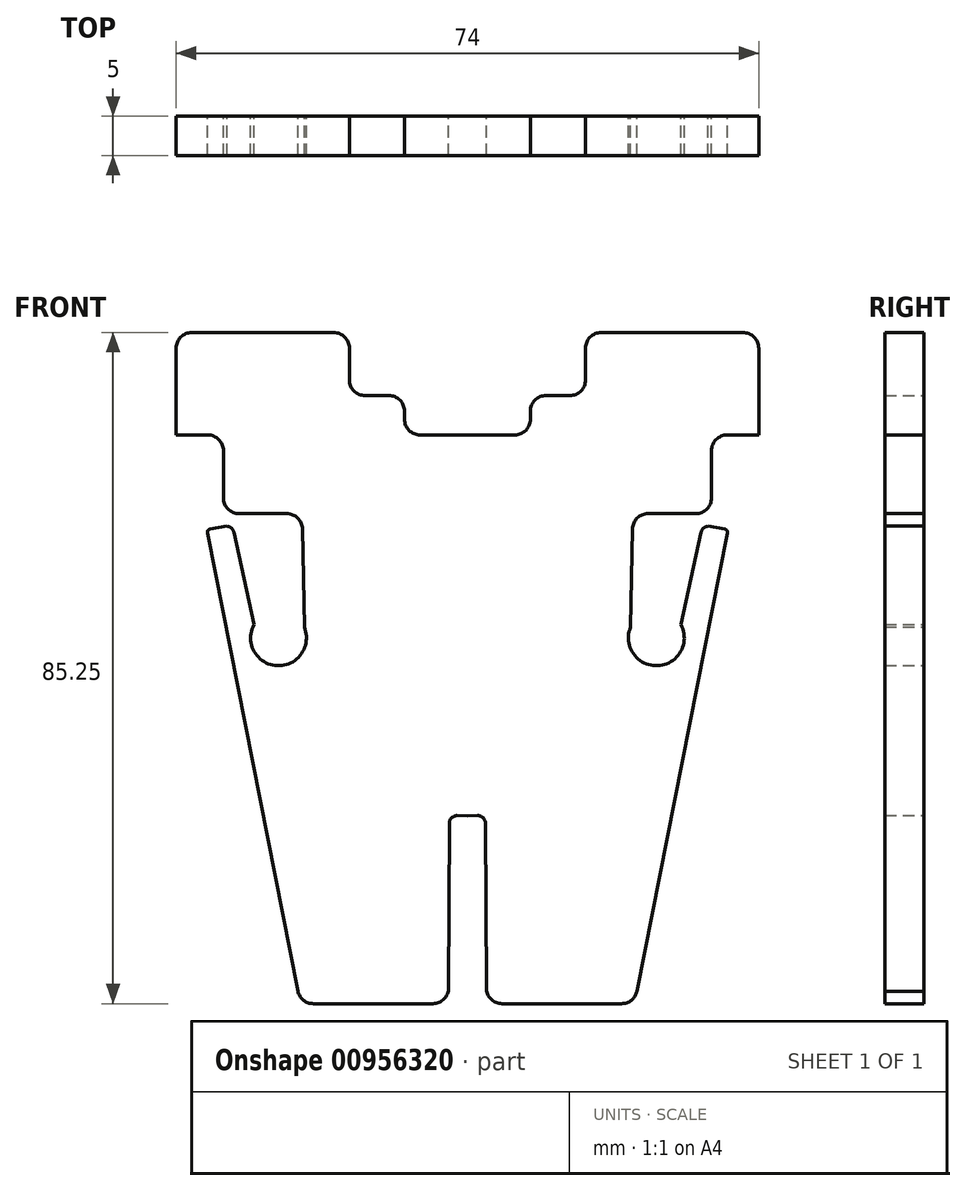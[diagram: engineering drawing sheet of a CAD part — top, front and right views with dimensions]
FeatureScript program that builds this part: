
annotation { "Feature Type Name" : "Feature", "Feature Type Description" : "" }
export const myFeature = defineFeature(function(context is Context, id is Id, definition is map)
    precondition{}
    {
        {
            var Q0;
            Q0=qCreatedBy(makeId("Front.planeOp"),FACE);
            var sketch = newSketch(context, id + "F0", { "sketchPlane" : qUnion([Q0])});
            skLineSegment(sketch, "E0", {"start": v(-4.4, -46.48) * mm, "end": v(-19.58, -46.48) * mm});
            skLineSegment(sketch, "E1", {"start": v(-22.96, 15.77) * mm, "end": v(-29, 15.77) * mm});
            skLineSegment(sketch, "E2", {"start": v(-31, 17.77) * mm, "end": v(-31, 23.77) * mm});
            skLineSegment(sketch, "E3", {"start": v(-33, 25.77) * mm, "end": v(-37, 25.77) * mm});
            skLineSegment(sketch, "E4", {"start": v(-37, 25.77) * mm, "end": v(-37, 36.77) * mm});
            skLineSegment(sketch, "E5", {"start": v(-35, 38.77) * mm, "end": v(-17, 38.77) * mm});
            skLineSegment(sketch, "E6", {"start": v(-15, 36.77) * mm, "end": v(-15, 32.77) * mm});
            skLineSegment(sketch, "E7", {"start": v(-13, 30.77) * mm, "end": v(-10, 30.77) * mm});
            skLineSegment(sketch, "E8", {"start": v(-8, 28.77) * mm, "end": v(-8, 27.77) * mm});
            skLineSegment(sketch, "E9", {"start": v(-6, 25.77) * mm, "end": v(0, 25.77) * mm});
            skLineSegment(sketch, "E10.MirrorCS", {"start": v(6, 25.77) * mm, "end": v(0, 25.77) * mm});
            skLineSegment(sketch, "E11.MirrorCS", {"start": v(13, 30.77) * mm, "end": v(10, 30.77) * mm});
            skLineSegment(sketch, "E12.MirrorCS", {"start": v(15, 36.77) * mm, "end": v(15, 32.77) * mm});
            skLineSegment(sketch, "E13.MirrorCS", {"start": v(35, 38.77) * mm, "end": v(17, 38.77) * mm});
            skLineSegment(sketch, "E14.MirrorCS", {"start": v(37, 25.77) * mm, "end": v(37, 36.77) * mm});
            skLineSegment(sketch, "E15.MirrorCS", {"start": v(22.96, 15.77) * mm, "end": v(29, 15.77) * mm});
            skLineSegment(sketch, "E16.MirrorCS", {"start": v(31, 17.77) * mm, "end": v(31, 23.77) * mm});
            skLineSegment(sketch, "E17.MirrorCS", {"start": v(33, 25.77) * mm, "end": v(37, 25.77) * mm});
            skLineSegment(sketch, "E18.MirrorCS", {"start": v(8, 28.77) * mm, "end": v(8, 27.77) * mm});
            skPoint(sketch, "E19.orphan", {"position": v(-2.04, -46.48) * mm});
            skPoint(sketch, "E20.MirrorCS.end.orphan", {"position": v(30.95, 9.46) * mm});
            skPoint(sketch, "E20.MirrorCS.start.orphan", {"position": v(20.96, -46.48) * mm});
            skPoint(sketch, "E21.orphan", {"position": v(-30.95, 9.46) * mm});
            skPoint(sketch, "E22.trimOffspring.end.orphan", {"position": v(20.62, -4.11) * mm});
            skLineSegment(sketch, "E23.trimOffspring", {"start": v(20.72, 1.3) * mm, "end": v(20.96, 13.81) * mm});
            skPoint(sketch, "E24.MirrorCS.start.orphan", {"position": v(20.73, -4.43) * mm});
            skPoint(sketch, "E25.orphan", {"position": v(-20.73, -4.43) * mm});
            skLineSegment(sketch, "E26.trimOffspring", {"start": v(-20.72, 1.3) * mm, "end": v(-20.96, 13.81) * mm});
            skPoint(sketch, "E27.start.orphan", {"position": v(-20.62, -4.11) * mm});
            skPoint(sketch, "E28.end.orphan", {"position": v(-20.7, -4.48) * mm});
            skPoint(sketch, "E29.MirrorCS.end.orphan", {"position": v(20.7, -4.48) * mm});
            skPoint(sketch, "E30.MirrorCS.start.orphan", {"position": v(-4, -24.4) * mm});
            skPoint(sketch, "E31.orphan", {"position": v(2.04, -46.48) * mm});
            skPoint(sketch, "E32.MirrorCS.start.orphan", {"position": v(0, -24.4) * mm});
            skPoint(sketch, "E33.end.orphan", {"position": v(4, -24.4) * mm});
            skArc(sketch, "E34", {"start": v(-27.13, 1.67) * mm, "mid": v(-24.16, -3.54) * mm, "end": v(-20.73, 1.37) * mm});
            skLineSegment(sketch, "E35.MirrorCS", {"start": v(27.13, 1.67) * mm, "end": v(27.1, 1.59) * mm});
            skArc(sketch, "E36.MirrorC", {"start": v(27.13, 1.67) * mm, "mid": v(24.16, -3.54) * mm, "end": v(20.73, 1.37) * mm});
            skPoint(sketch, "E37.visualSharp", {"position": v(-37, 38.77) * mm});
            skArc(sketch, "E37.filletArc", {"start": v(-35, 38.77) * mm, "mid": v(-36.41, 38.19) * mm, "end": v(-37, 36.77) * mm});
            skPoint(sketch, "E38.visualSharp", {"position": v(-15, 38.77) * mm});
            skArc(sketch, "E38.filletArc", {"start": v(-15, 36.77) * mm, "mid": v(-15.59, 38.19) * mm, "end": v(-17, 38.77) * mm});
            skPoint(sketch, "E39.visualSharp", {"position": v(-15, 30.77) * mm});
            skArc(sketch, "E39.filletArc", {"start": v(-15, 32.77) * mm, "mid": v(-14.41, 31.36) * mm, "end": v(-13, 30.77) * mm});
            skPoint(sketch, "E40.visualSharp", {"position": v(-8, 30.77) * mm});
            skArc(sketch, "E40.filletArc", {"start": v(-8, 28.77) * mm, "mid": v(-8.59, 30.19) * mm, "end": v(-10, 30.77) * mm});
            skPoint(sketch, "E41.visualSharp", {"position": v(-8, 25.77) * mm});
            skArc(sketch, "E41.filletArc", {"start": v(-8, 27.77) * mm, "mid": v(-7.41, 26.36) * mm, "end": v(-6, 25.77) * mm});
            skPoint(sketch, "E42.visualSharp", {"position": v(8, 25.77) * mm});
            skArc(sketch, "E42.filletArc", {"start": v(6, 25.77) * mm, "mid": v(7.41, 26.36) * mm, "end": v(8, 27.77) * mm});
            skPoint(sketch, "E43.visualSharp", {"position": v(8, 30.77) * mm});
            skArc(sketch, "E43.filletArc", {"start": v(10, 30.77) * mm, "mid": v(8.59, 30.19) * mm, "end": v(8, 28.77) * mm});
            skPoint(sketch, "E44.visualSharp", {"position": v(15, 30.77) * mm});
            skArc(sketch, "E44.filletArc", {"start": v(13, 30.77) * mm, "mid": v(14.41, 31.36) * mm, "end": v(15, 32.77) * mm});
            skPoint(sketch, "E45.visualSharp", {"position": v(15, 38.77) * mm});
            skArc(sketch, "E45.filletArc", {"start": v(17, 38.77) * mm, "mid": v(15.59, 38.19) * mm, "end": v(15, 36.77) * mm});
            skPoint(sketch, "E46.visualSharp", {"position": v(37, 38.77) * mm});
            skArc(sketch, "E46.filletArc", {"start": v(37, 36.77) * mm, "mid": v(36.41, 38.19) * mm, "end": v(35, 38.77) * mm});
            skPoint(sketch, "E47.visualSharp", {"position": v(31, 25.77) * mm});
            skArc(sketch, "E47.filletArc", {"start": v(33, 25.77) * mm, "mid": v(31.59, 25.19) * mm, "end": v(31, 23.77) * mm});
            skPoint(sketch, "E48.visualSharp", {"position": v(-31, 25.77) * mm});
            skArc(sketch, "E48.filletArc", {"start": v(-31, 23.77) * mm, "mid": v(-31.59, 25.19) * mm, "end": v(-33, 25.77) * mm});
            skPoint(sketch, "E49.visualSharp", {"position": v(-31, 15.77) * mm});
            skArc(sketch, "E49.filletArc", {"start": v(-31, 17.77) * mm, "mid": v(-30.41, 16.36) * mm, "end": v(-29, 15.77) * mm});
            skPoint(sketch, "E50.visualSharp", {"position": v(31, 15.77) * mm});
            skArc(sketch, "E50.filletArc", {"start": v(29, 15.77) * mm, "mid": v(30.41, 16.36) * mm, "end": v(31, 17.77) * mm});
            skPoint(sketch, "E51.visualSharp", {"position": v(21, 15.77) * mm});
            skArc(sketch, "E51.filletArc", {"start": v(22.96, 15.77) * mm, "mid": v(21.56, 15.2) * mm, "end": v(20.96, 13.81) * mm});
            skPoint(sketch, "E52.visualSharp", {"position": v(-21, 15.77) * mm});
            skArc(sketch, "E52.filletArc", {"start": v(-20.96, 13.81) * mm, "mid": v(-21.56, 15.2) * mm, "end": v(-22.96, 15.77) * mm});
            skPoint(sketch, "E53.visualSharp", {"position": v(29.73, 12.95) * mm});
            skPoint(sketch, "E54.visualSharp", {"position": v(34.13, 12.77) * mm});
            skPoint(sketch, "E55.visualSharp", {"position": v(-29.73, 12.95) * mm});
            skPoint(sketch, "E56.visualSharp", {"position": v(-34.13, 12.77) * mm});
            skPoint(sketch, "E57.visualSharp", {"position": v(-20.96, -46.48) * mm});
            skArc(sketch, "E57.filletArc", {"start": v(-21.53, -44.9) * mm, "mid": v(-20.83, -46.04) * mm, "end": v(-19.58, -46.48) * mm});
            skArc(sketch, "E58.filletArc", {"start": v(-4.4, -46.48) * mm, "mid": v(-2.98, -45.9) * mm, "end": v(-2.4, -44.48) * mm});
            skPoint(sketch, "E59.visualSharp", {"position": v(-2.2, -23.84) * mm});
            skPoint(sketch, "E60.end.orphan", {"position": v(-1.93, -24.4) * mm});
            skPoint(sketch, "E61.visualSharp", {"position": v(-34.6, 14.93) * mm});
            skLineSegment(sketch, "E62", {"start": v(-27.13, 1.67) * mm, "end": v(-29.68, 13.4) * mm});
            skPoint(sketch, "E63.visualSharp", {"position": v(-29.73, 13.64) * mm});
            skPoint(sketch, "E64.visualSharp", {"position": v(-34.39, 13.95) * mm});
            skPoint(sketch, "E65.visualSharp", {"position": v(-30.1, 15.35) * mm});
            skArc(sketch, "E65.filletArc", {"start": v(-29.68, 13.4) * mm, "mid": v(-29.98, 13.92) * mm, "end": v(-30.54, 14.17) * mm});
            skPoint(sketch, "E59.filletArc.end.orphan", {"position": v(-4.18, -23.84) * mm});
            skPoint(sketch, "E66.MirrorCS.end.orphan", {"position": v(4.18, -23.84) * mm});
            skPoint(sketch, "E66.MirrorCS.start.orphan", {"position": v(2.3, -25.82) * mm});
            skPoint(sketch, "E67.MirrorCS.end.orphan", {"position": v(1.95, -45.25) * mm});
            skPoint(sketch, "E68.end.orphan", {"position": v(-1.95, -45.25) * mm});
            skPoint(sketch, "E68.start.orphan", {"position": v(-2.3, -25.82) * mm});
            skLineSegment(sketch, "E69", {"start": v(-2.4, -44.48) * mm, "end": v(-2.3, -23.59) * mm});
            skLineSegment(sketch, "E70", {"start": v(-1.3, -22.6) * mm, "end": v(0, -22.6) * mm});
            skLineSegment(sketch, "E71.MirrorCS", {"start": v(1.3, -22.6) * mm, "end": v(0, -22.6) * mm});
            skPoint(sketch, "E72.MirrorP", {"position": v(1.93, -24.4) * mm});
            skLineSegment(sketch, "E73.MirrorCS", {"start": v(2.4, -44.48) * mm, "end": v(2.3, -23.59) * mm});
            skArc(sketch, "E74.MirrorCS", {"start": v(4.4, -46.48) * mm, "mid": v(2.98, -45.9) * mm, "end": v(2.4, -44.48) * mm});
            skLineSegment(sketch, "E75.MirrorCS", {"start": v(4.4, -46.48) * mm, "end": v(19.58, -46.48) * mm});
            skPoint(sketch, "E76.visualSharp", {"position": v(-2.3, -22.59) * mm});
            skArc(sketch, "E76.filletArc", {"start": v(-1.3, -22.6) * mm, "mid": v(-2.01, -22.88) * mm, "end": v(-2.3, -23.59) * mm});
            skPoint(sketch, "E77.visualSharp", {"position": v(2.3, -22.59) * mm});
            skArc(sketch, "E77.filletArc", {"start": v(2.3, -23.59) * mm, "mid": v(2.01, -22.88) * mm, "end": v(1.3, -22.6) * mm});
            skPoint(sketch, "E64.filletArc.end.orphan", {"position": v(-34.24, 13.28) * mm});
            skPoint(sketch, "E64.filletArc.start.orphan", {"position": v(-33.1, 14.5) * mm});
            skLineSegment(sketch, "E78", {"start": v(-21.53, -44.9) * mm, "end": v(-33.03, 13.33) * mm});
            skLineSegment(sketch, "E79", {"start": v(-32.7, 13.8) * mm, "end": v(-30.54, 14.17) * mm});
            skPoint(sketch, "E80.MirrorCS.end.orphan", {"position": v(29.68, 13.4) * mm});
            skPoint(sketch, "E80.MirrorCS.start.orphan", {"position": v(27.13, 1.67) * mm});
            skPoint(sketch, "E81.MirrorCS.end.orphan", {"position": v(30.54, 14.17) * mm});
            skPoint(sketch, "E82.MirrorCS.start.orphan", {"position": v(33.1, 14.5) * mm});
            skPoint(sketch, "E83.MirrorCS.end.orphan", {"position": v(34.24, 13.28) * mm});
            skPoint(sketch, "E84.orphan", {"position": v(21.53, -44.9) * mm});
            skLineSegment(sketch, "E85.MirrorCS", {"start": v(27.13, 1.67) * mm, "end": v(29.68, 13.4) * mm});
            skArc(sketch, "E86.MirrorCS", {"start": v(29.68, 13.4) * mm, "mid": v(29.98, 13.92) * mm, "end": v(30.54, 14.17) * mm});
            skLineSegment(sketch, "E87.MirrorCS", {"start": v(32.7, 13.8) * mm, "end": v(30.54, 14.17) * mm});
            skLineSegment(sketch, "E88.MirrorCS", {"start": v(21.53, -44.9) * mm, "end": v(33.03, 13.33) * mm});
            skArc(sketch, "E89.MirrorCS", {"start": v(21.53, -44.9) * mm, "mid": v(20.83, -46.04) * mm, "end": v(19.58, -46.48) * mm});
            skPoint(sketch, "E90.visualSharp", {"position": v(-33.1, 13.73) * mm});
            skArc(sketch, "E90.filletArc", {"start": v(-32.7, 13.8) * mm, "mid": v(-32.96, 13.63) * mm, "end": v(-33.03, 13.33) * mm});
            skPoint(sketch, "E91.visualSharp", {"position": v(33.1, 13.73) * mm});
            skArc(sketch, "E91.filletArc", {"start": v(33.03, 13.33) * mm, "mid": v(32.96, 13.63) * mm, "end": v(32.7, 13.8) * mm});
            skSolve(sketch);
        }
        {
            var Q0;
            Q0 = qSketchRegion(id + "F0", true);
            extrude(context, id + "F1", {"entities" : qUnion([Q0]), "depth" : 5 * mm, "offsetDistance" : 25 * mm});
        }
    });
